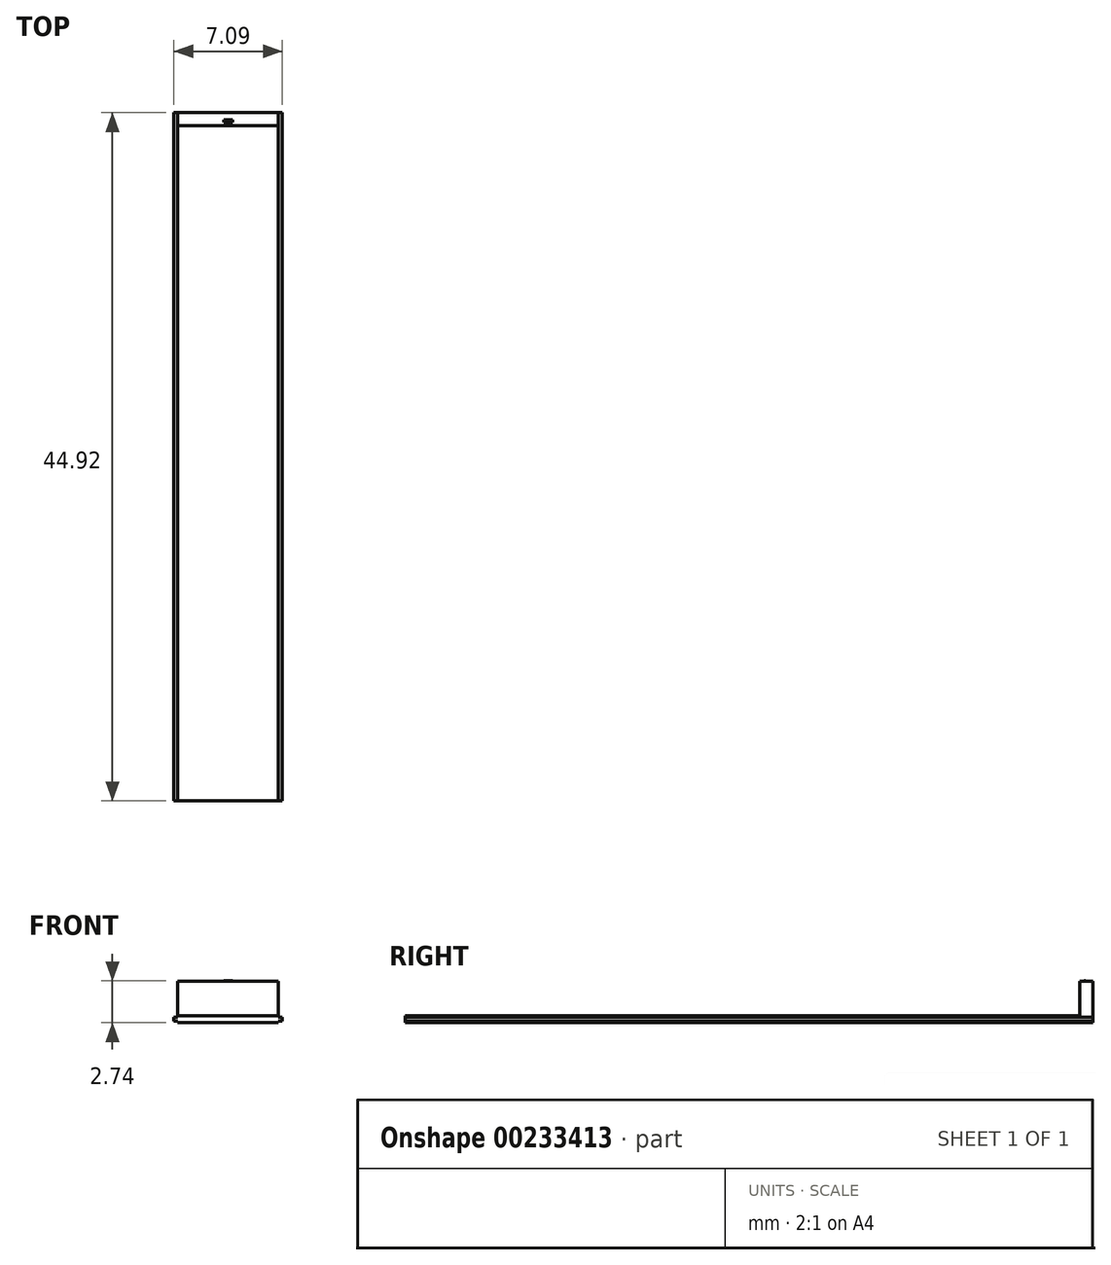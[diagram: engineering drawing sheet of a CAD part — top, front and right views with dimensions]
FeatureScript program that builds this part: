
annotation { "Feature Type Name" : "Feature", "Feature Type Description" : "" }
export const myFeature = defineFeature(function(context is Context, id is Id, definition is map)
    precondition{}
    {
        {
            var Q0;
            Q0=qCreatedBy(makeId("Front.planeOp"),FACE);
            var sketch = newSketch(context, id + "F3", { "sketchPlane" : qUnion([Q0])});
            skLineSegment(sketch, "E0", {"start": v(-2.78, 0.27) * mm, "end": v(-2.78, -0.2) * mm});
            skLineSegment(sketch, "E1", {"start": v(-2.78, 0.27) * mm, "end": v(3.8, 0.27) * mm});
            skLineSegment(sketch, "E2", {"start": v(3.8, 0.27) * mm, "end": v(3.8, -0.2) * mm});
            skLineSegment(sketch, "E3", {"start": v(3.8, -0.2) * mm, "end": v(-2.78, -0.2) * mm});
            skLineSegment(sketch, "E4.bottom", {"start": v(4.05, -0.08) * mm, "end": v(-3.04, -0.08) * mm});
            skLineSegment(sketch, "E4.top", {"start": v(4.05, 0.15) * mm, "end": v(-3.04, 0.15) * mm});
            skLineSegment(sketch, "E4.left", {"start": v(4.05, -0.08) * mm, "end": v(4.05, 0.15) * mm});
            skLineSegment(sketch, "E4.right", {"start": v(-3.04, -0.08) * mm, "end": v(-3.04, 0.15) * mm});
            skPoint(sketch, "E4.middle", {"position": v(0.5, 0.04) * mm});
            skPoint(sketch, "E4.middle.positionSnap0", {"position": v(0.5, -0.2) * mm});
            skPoint(sketch, "E4.middle.positionSnap1", {"position": v(-2.78, 0.04) * mm});
            skPoint(sketch, "E4.centerSnap0", {"position": v(0.5, -0.2) * mm});
            skPoint(sketch, "E4.centerSnap1", {"position": v(-2.78, 0.04) * mm});
            skSolve(sketch);
        }
        {
            var Q0;
            {var subQ0=sQuery(id+"F3.wireOp",EDGE,"E4.top");var subQ1=sQuery(id+"F3.wireOp",EDGE,"E0");var subQ2=makeQuery(id+"F3.imprint","INTERSECT",VERTEX,{"derivedFrom":[subQ1,subQ0]});Q0=makeQuery(id+"F3.imprint","IMPRINT",FACE,{"disambiguationData":[TD([[makeQuery(id+"F3.imprint","IMPRINT",EDGE,{"disambiguationData":[TD([[subQ2,-1.0]])],"derivedFrom":subQ1}),1.0]])]});}
            var Q1;
            {var subQ0=sQuery(id+"F3.wireOp",EDGE,"E1");Q1=makeQuery(id+"F3.imprint","IMPRINT",FACE,{"disambiguationData":[TD([[makeQuery(id+"F3.imprint","IMPRINT",EDGE,{"derivedFrom":subQ0}),-1.0]])]});}
            var Q2;
            {var subQ0=sQuery(id+"F3.wireOp",EDGE,"E3");Q2=makeQuery(id+"F3.imprint","IMPRINT",FACE,{"disambiguationData":[TD([[makeQuery(id+"F3.imprint","IMPRINT",EDGE,{"derivedFrom":subQ0}),-1.0]])]});}
            var Q3;
            {var subQ5=sQuery(id+"F3.wireOp",EDGE,"E4.right");Q3=makeQuery(id+"F3.imprint","IMPRINT",FACE,{"disambiguationData":[TD([[makeQuery(id+"F3.imprint","IMPRINT",EDGE,{"derivedFrom":subQ5}),-1.0]])]});}
            var Q4;
            {var subQ5=sQuery(id+"F3.wireOp",EDGE,"E4.left");Q4=makeQuery(id+"F3.imprint","IMPRINT",FACE,{"disambiguationData":[TD([[makeQuery(id+"F3.imprint","IMPRINT",EDGE,{"derivedFrom":subQ5}),1.0]])]});}
            extrude(context, id + "F4", {"entities" : qUnion([Q0, Q1, Q2, Q3, Q4]), "depth" : 44.92 * mm});
        }
        {
            var Q0;
            Q0=makeQuery(id+"F4.opExtrude","SWEPT_FACE",FACE,{"disambiguationData":[OSD([sQuery(id+"F3.wireOp",EDGE,"E1")])]});
            var sketch = newSketch(context, id + "F0", { "sketchPlane" : qUnion([Q0])});
            skLineSegment(sketch, "E5.bottom", {"start": v(3.8, -0.86) * mm, "end": v(-2.78, -0.86) * mm});
            skLineSegment(sketch, "E5.top", {"start": v(3.8, 0) * mm, "end": v(-2.78, 0) * mm});
            skLineSegment(sketch, "E5.left", {"start": v(3.8, -0.86) * mm, "end": v(3.8, 0) * mm});
            skLineSegment(sketch, "E5.right", {"start": v(-2.78, -0.86) * mm, "end": v(-2.78, 0) * mm});
            skPoint(sketch, "E5.middle", {"position": v(0.5, -0.43) * mm});
            skPoint(sketch, "E5.middle.positionSnap0", {"position": v(0.5, 0) * mm});
            skPoint(sketch, "E5.centerSnap0", {"position": v(0.5, 0) * mm});
            skSolve(sketch);
        }
        {
            var Q0;
            Q0=makeQuery(id+"F0.imprint","IMPRINT",FACE,{"disambiguationData":[TD([[makeQuery(id+"F0.imprint","IMPRINT",EDGE,{"derivedFrom":sQuery(id+"F0.wireOp",EDGE,"E5.bottom")}),-1.0]])]});
            extrude(context, id + "F1", {"entities" : qUnion([Q0]), "operationType" : NewBodyOperationType.ADD, "depth" : 2.24 * mm});
        }
        {
            var Q0;
            Q0=makeQuery(id+"F1.opExtrude","CAP_FACE",FACE,{"disambiguationData":[OSD([sQuery(id+"F0.wireOp",EDGE,"E5.bottom"),sQuery(id+"F0.wireOp",EDGE,"E5.top"),sQuery(id+"F0.wireOp",EDGE,"E5.left"),sQuery(id+"F0.wireOp",EDGE,"E5.right")])],"isStart":false});
            var sketch = newSketch(context, id + "F5", { "sketchPlane" : qUnion([Q0])});
            skLineSegment(sketch, "E6.bottom", {"start": v(0.8, -0.61) * mm, "end": v(0.2, -0.61) * mm});
            skLineSegment(sketch, "E6.top", {"start": v(0.8, -0.24) * mm, "end": v(0.2, -0.24) * mm});
            skLineSegment(sketch, "E6.left", {"start": v(0.8, -0.61) * mm, "end": v(0.8, -0.24) * mm});
            skLineSegment(sketch, "E6.right", {"start": v(0.2, -0.61) * mm, "end": v(0.2, -0.24) * mm});
            skPoint(sketch, "E6.middle", {"position": v(0.5, -0.43) * mm});
            skPoint(sketch, "E6.middle.positionSnap0", {"position": v(3.8, -0.43) * mm});
            skPoint(sketch, "E6.middle.positionSnap1", {"position": v(0.5, -0.86) * mm});
            skPoint(sketch, "E6.centerSnap0", {"position": v(3.8, -0.43) * mm});
            skPoint(sketch, "E6.centerSnap1", {"position": v(0.5, -0.86) * mm});
            skSolve(sketch);
        }
        {
            var Q0;
            Q0=makeQuery(id+"F5.imprint","IMPRINT",FACE,{"disambiguationData":[TD([[makeQuery(id+"F5.imprint","IMPRINT",EDGE,{"derivedFrom":sQuery(id+"F5.wireOp",EDGE,"E6.bottom")}),-1.0]])]});
            extrude(context, id + "F6", {"entities" : qUnion([Q0]), "operationType" : NewBodyOperationType.ADD, "depth" : 0.03 * mm});
        }
        {
            var Q0;
            Q0=makeQuery(id+"F6.opExtrude","CAP_EDGE",EDGE,{"disambiguationData":[OSD([sQuery(id+"F5.wireOp",EDGE,"E6.top")])],"isStart":false});
            chamfer(context, id + "F7", {"entities" : qUnion([Q0]), "width" : 0.25 * mm, "tangentPropagation" : true});
        }
        {
            var Q0;
            Q0=makeQuery(id+"F6.opExtrude","CAP_EDGE",EDGE,{"disambiguationData":[OSD([sQuery(id+"F5.wireOp",EDGE,"E6.bottom")])],"isStart":false});
            chamfer(context, id + "F2", {"entities" : qUnion([Q0]), "width" : 0.03 * mm, "tangentPropagation" : true});
        }
    });
